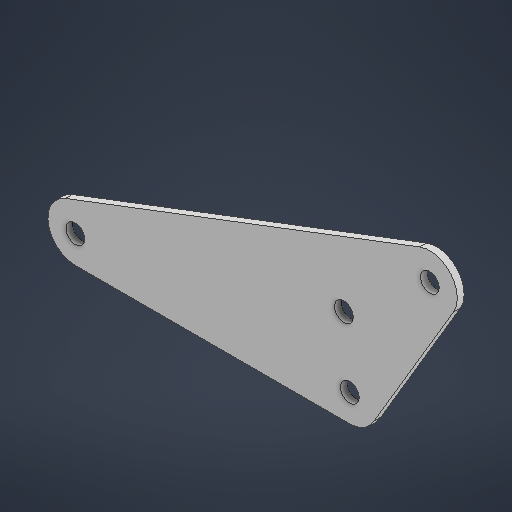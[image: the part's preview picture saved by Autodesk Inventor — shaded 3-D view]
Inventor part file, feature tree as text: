
AUTODESK INVENTOR PART (.ipt)
format: ipt  version: 2025.2 (Build 292293000, 293)  size: 187,392 bytes
history: native  units: in
note: dims shown in document units (in); Inventor stores cm internally (conversion verified against a paired STEP export)
features: extrude x1, sketch x1
ambient origin geometry x8: Origin, YZ Plane, XZ Plane, XY Plane, X Axis, Y Axis, Z Axis, Center Point
bodies: Solid1 (feature_tree)
feature tree (2):
  extrude  "Extrusion1"  Depth=0.0625in TaperAngle=0.0deg
  sketch  "Sketch1"  dims[d0=0.5in d1=0.5in d2=0.5in d3=0.0625in d4=0.0in]
